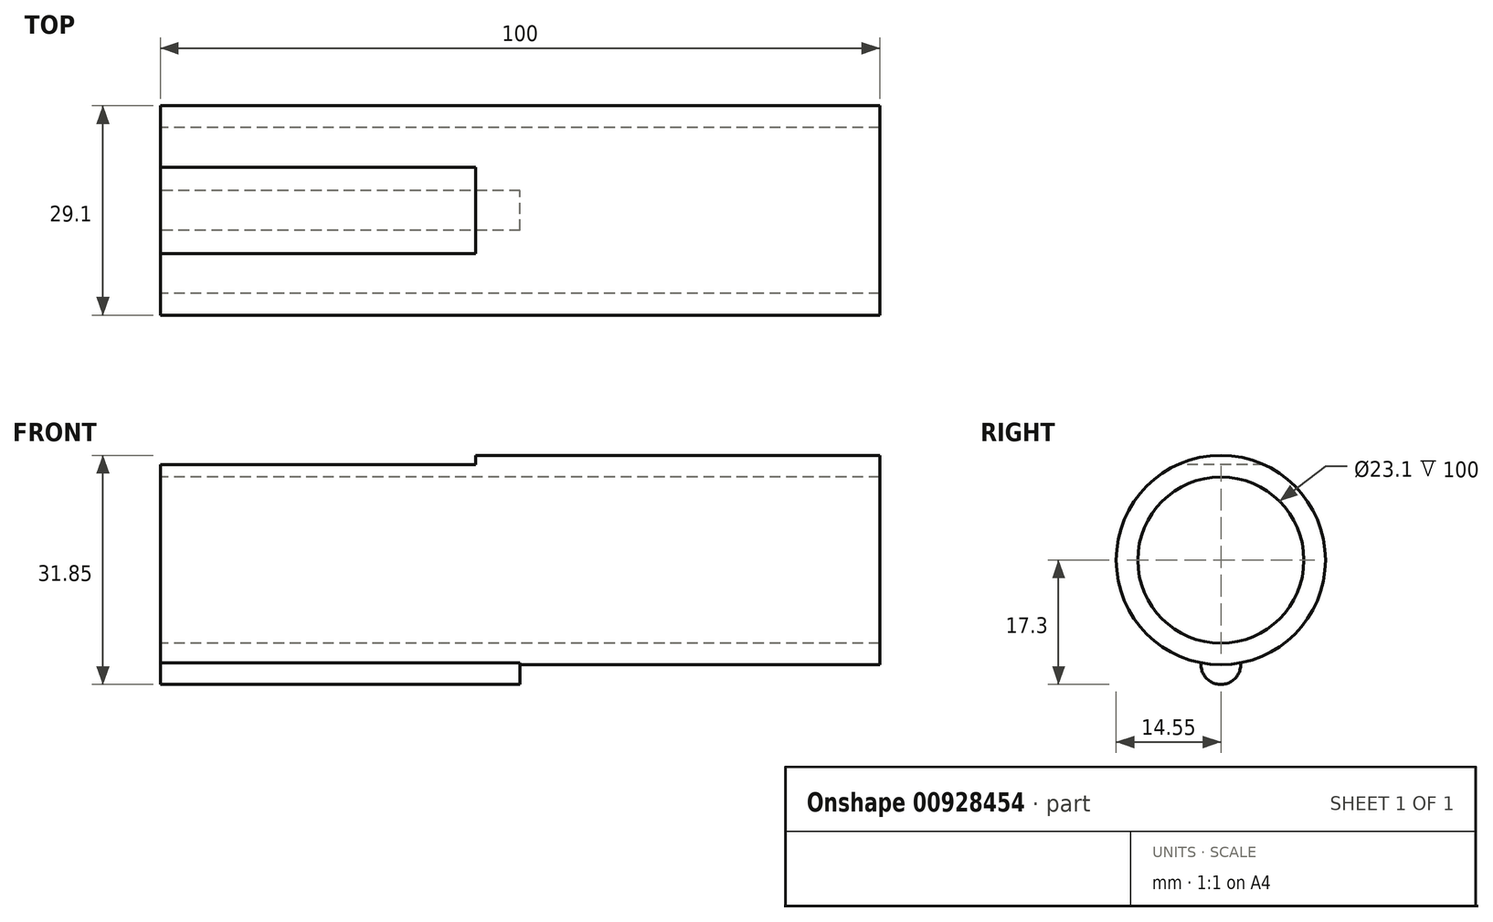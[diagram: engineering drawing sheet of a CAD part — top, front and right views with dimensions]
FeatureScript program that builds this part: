
annotation { "Feature Type Name" : "Feature", "Feature Type Description" : "" }
export const myFeature = defineFeature(function(context is Context, id is Id, definition is map)
    precondition{}
    {
        {
            var Q0;
            Q0=qCreatedBy(makeId("Front.planeOp"),FACE);
            var sketch = newSketch(context, id + "F0", { "sketchPlane" : qUnion([Q0])});
            skLineSegment(sketch, "E0", {"start": v(-35.95, 0) * mm, "end": v(38.01, 0) * mm, "construction": true});
            skLineSegment(sketch, "E1.bottom", {"start": v(0, 11.55) * mm, "end": v(100, 11.55) * mm});
            skLineSegment(sketch, "E1.top", {"start": v(0, 14.55) * mm, "end": v(100, 14.55) * mm});
            skLineSegment(sketch, "E1.left", {"start": v(0, 11.55) * mm, "end": v(0, 14.55) * mm});
            skLineSegment(sketch, "E1.right", {"start": v(100, 11.55) * mm, "end": v(100, 14.55) * mm});
            skSolve(sketch);
        }
        {
            var Q0;
            Q0 = qSketchRegion(id + "F0", true);
            var Q1;
            Q1=sQuery(id+"F0.wireOp",EDGE,"E0");
            revolve(context, id + "F1", {"surfaceOperationType" : NewSurfaceOperationType.NEW, "entities" : qUnion([Q0]), "axis" : qUnion([Q1]), "revolveType" : RevolveType.FULL});
        }
        {
            var Q0;
            Q0=qCreatedBy(makeId("Right.planeOp"),FACE);
            var sketch = newSketch(context, id + "F2", { "sketchPlane" : qUnion([Q0])});
            skLineSegment(sketch, "E2.bottom", {"start": v(6, 13.26) * mm, "end": v(-6, 13.26) * mm});
            skLineSegment(sketch, "E2.top", {"start": v(6, 18.26) * mm, "end": v(-6, 18.26) * mm});
            skLineSegment(sketch, "E2.left", {"start": v(6, 13.26) * mm, "end": v(6, 18.26) * mm});
            skLineSegment(sketch, "E2.right", {"start": v(-6, 13.26) * mm, "end": v(-6, 18.26) * mm});
            skSolve(sketch);
        }
        {
            var Q0;
            Q0 = qSketchRegion(id + "F2", true);
            extrude(context, id + "F3", {"entities" : qUnion([Q0]), "operationType" : NewBodyOperationType.REMOVE, "depth" : 43.86 * mm, "offsetDistance" : 25 * mm});
        }
        {
            var Q0;
            Q0=qCreatedBy(makeId("Right.planeOp"),FACE);
            var sketch = newSketch(context, id + "F4", { "sketchPlane" : qUnion([Q0])});
            skCircle(sketch, "E3", {"center": v(0, -14.55) * mm, "radius": 2.75 * mm});
            skSolve(sketch);
        }
        {
            var Q0;
            Q0 = qSketchRegion(id + "F4", true);
            extrude(context, id + "F5", {"entities" : qUnion([Q0]), "operationType" : NewBodyOperationType.ADD, "depth" : 50 * mm, "offsetDistance" : 25 * mm});
        }
    });
